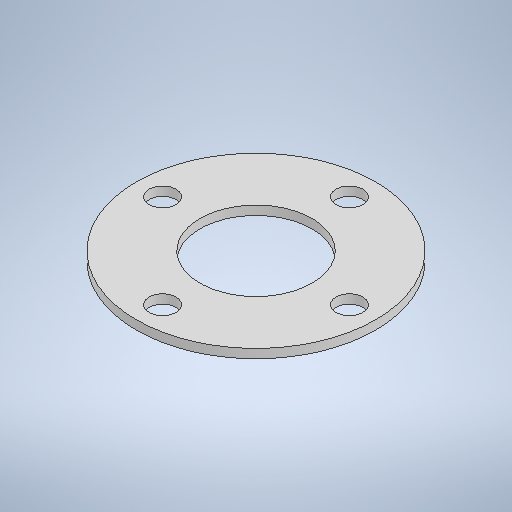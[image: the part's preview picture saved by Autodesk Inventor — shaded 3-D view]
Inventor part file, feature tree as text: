
AUTODESK INVENTOR PART (.ipt)
format: ipt  version: 2025.4 (Build 294407000, 407)  size: 292,352 bytes
history: native  units: mm
features: sketch x2, other x2, sheet_metal_op x1
ambient origin geometry x8: Origin, YZ Plane, XZ Plane, XY Plane, X Axis, Y Axis, Z Axis, Center Point
bodies: Body1 (feature_tree)
feature tree (5):
  sheet_metal_op  "Face2"
  sketch  "Sketch2"  dims[d25=75.0mm d27=160.0mm d29=125.0mm d30=18.0mm d31=40.0mm d33=360.0deg]
  other  "Plate2"
  sketch  "Sketch Circular Pattern1"  dims[d14=6.0mm]
  other  "Definition1"
